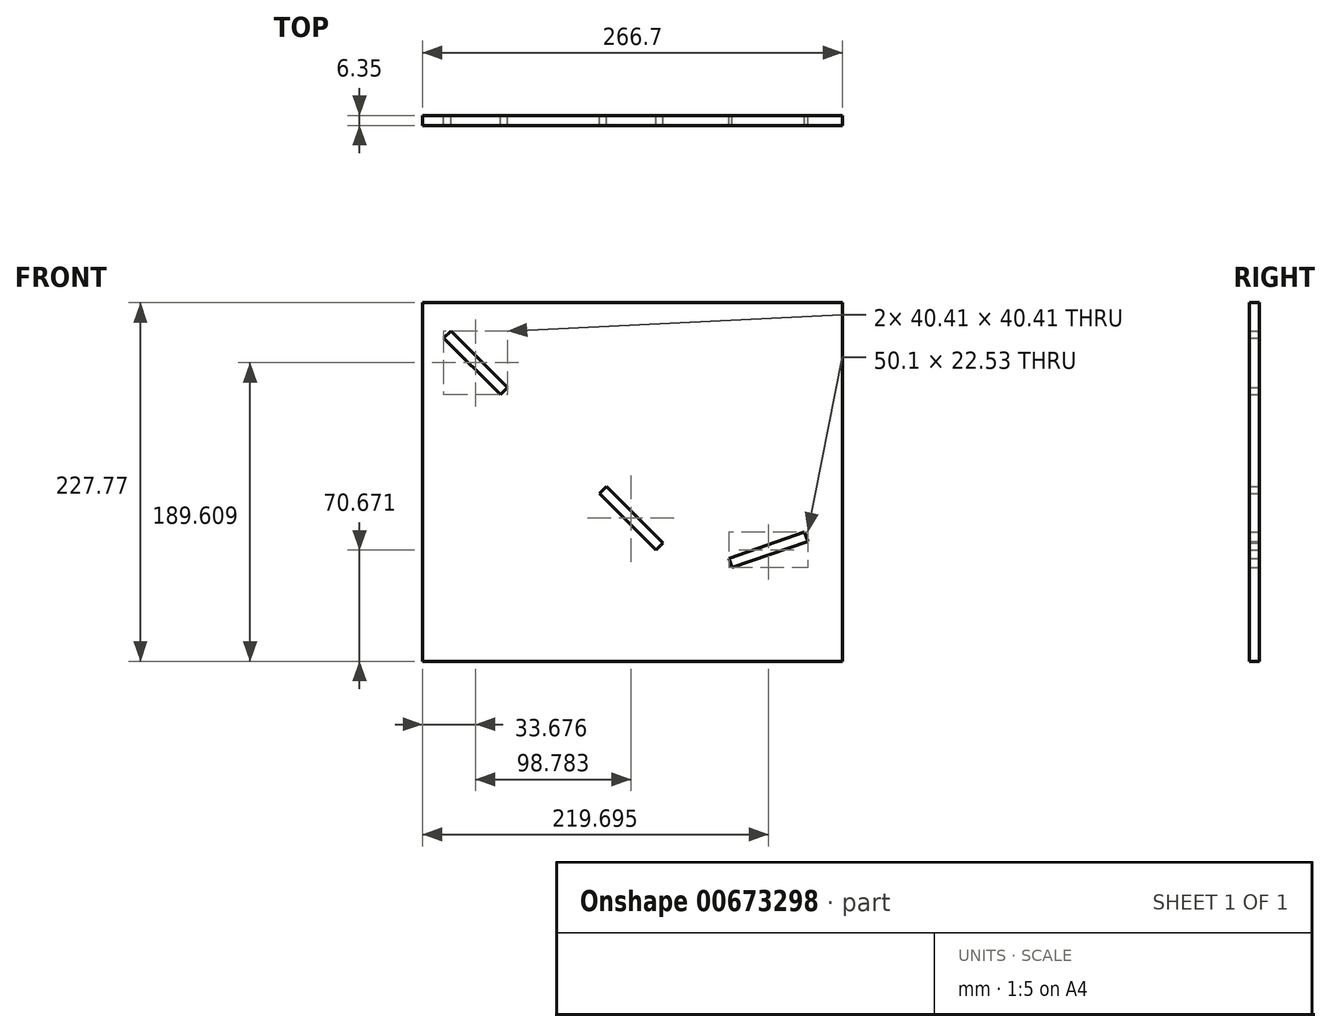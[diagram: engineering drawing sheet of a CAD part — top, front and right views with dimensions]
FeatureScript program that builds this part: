
annotation { "Feature Type Name" : "Feature", "Feature Type Description" : "" }
export const myFeature = defineFeature(function(context is Context, id is Id, definition is map)
    precondition{}
    {
        {
            var Q0;
            Q0=qCreatedBy(makeId("Front.planeOp"),FACE);
            var sketch = newSketch(context, id + "F0", { "sketchPlane" : qUnion([Q0])});
            skLineSegment(sketch, "E0.bottom", {"start": v(-133.35, 227.77) * mm, "end": v(133.35, 227.77) * mm});
            skLineSegment(sketch, "E0.top", {"start": v(-133.35, 0) * mm, "end": v(133.35, 0) * mm});
            skLineSegment(sketch, "E0.left", {"start": v(-133.35, 227.77) * mm, "end": v(-133.35, 0) * mm});
            skLineSegment(sketch, "E0.right", {"start": v(133.35, 227.77) * mm, "end": v(133.35, 0) * mm});
            skLineSegment(sketch, "E1", {"start": v(37.27, 57.15) * mm, "end": v(133.35, 90.2) * mm, "construction": true});
            skLineSegment(sketch, "E2", {"start": v(37.27, 57.15) * mm, "end": v(-133.35, 227.77) * mm, "construction": true});
            skLineSegment(sketch, "E3", {"start": v(61.3, 65.41) * mm, "end": v(109.33, 81.94) * mm});
            skLineSegment(sketch, "E4", {"start": v(109.33, 81.94) * mm, "end": v(111.4, 75.93) * mm});
            skLineSegment(sketch, "E5", {"start": v(111.4, 75.93) * mm, "end": v(63.36, 59.4) * mm});
            skLineSegment(sketch, "E6", {"start": v(63.36, 59.4) * mm, "end": v(61.3, 65.41) * mm});
            skLineSegment(sketch, "E7", {"start": v(-115.39, 209.81) * mm, "end": v(-119.88, 205.32) * mm});
            skLineSegment(sketch, "E8", {"start": v(-119.88, 205.32) * mm, "end": v(-83.96, 169.4) * mm});
            skLineSegment(sketch, "E9", {"start": v(-83.96, 169.4) * mm, "end": v(-79.47, 173.9) * mm});
            skLineSegment(sketch, "E10", {"start": v(-79.47, 173.9) * mm, "end": v(-115.39, 209.81) * mm});
            skLineSegment(sketch, "E11", {"start": v(19.31, 75.11) * mm, "end": v(14.82, 70.62) * mm});
            skLineSegment(sketch, "E12", {"start": v(14.82, 70.62) * mm, "end": v(-21.1, 106.54) * mm});
            skLineSegment(sketch, "E13", {"start": v(-21.1, 106.54) * mm, "end": v(-16.6, 111.03) * mm});
            skLineSegment(sketch, "E14", {"start": v(-16.6, 111.03) * mm, "end": v(19.31, 75.11) * mm});
            skSolve(sketch);
        }
        {
            var Q0;
            Q0 = qSketchRegion(id + "F0", true);
            extrude(context, id + "F1", {"entities" : qUnion([Q0]), "depth" : 6.35 * mm, "offsetDistance" : 25.4 * mm});
        }
    });
